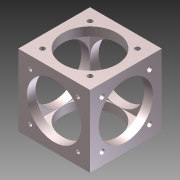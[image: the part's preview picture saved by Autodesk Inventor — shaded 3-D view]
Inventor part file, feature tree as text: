
AUTODESK INVENTOR PART (.ipt)
format: ipt  version: 2012 SP2 (Build 160219200, 219)  size: 205,824 bytes
history: native  units: mm
features: thread x4, other x2
ambient origin geometry x8: Origin, YZ Plane, XZ Plane, XY Plane, X Axis, Y Axis, Z Axis, Center Point
bodies: Solid1 (feature_tree)
feature tree (6):
  other  "X95_corner_cube.iam"
  other  "00011479.ipt:1"
  thread  "GEWINDEHUELSE.ipt:1"  [1 undecoded]
  thread  "GEWINDEHUELSE_1.ipt:1"  [1 undecoded]
  thread  "GEWINDEHUELSE_2.ipt:1"  [1 undecoded]
  thread  "GEWINDEHUELSE_3.ipt:1"  [1 undecoded]
note: 4 required parameter values undecoded (feature->parameter linkage not recoverable at this tier; creation-order binding heuristic only, values carry confidence <= 0.55)
